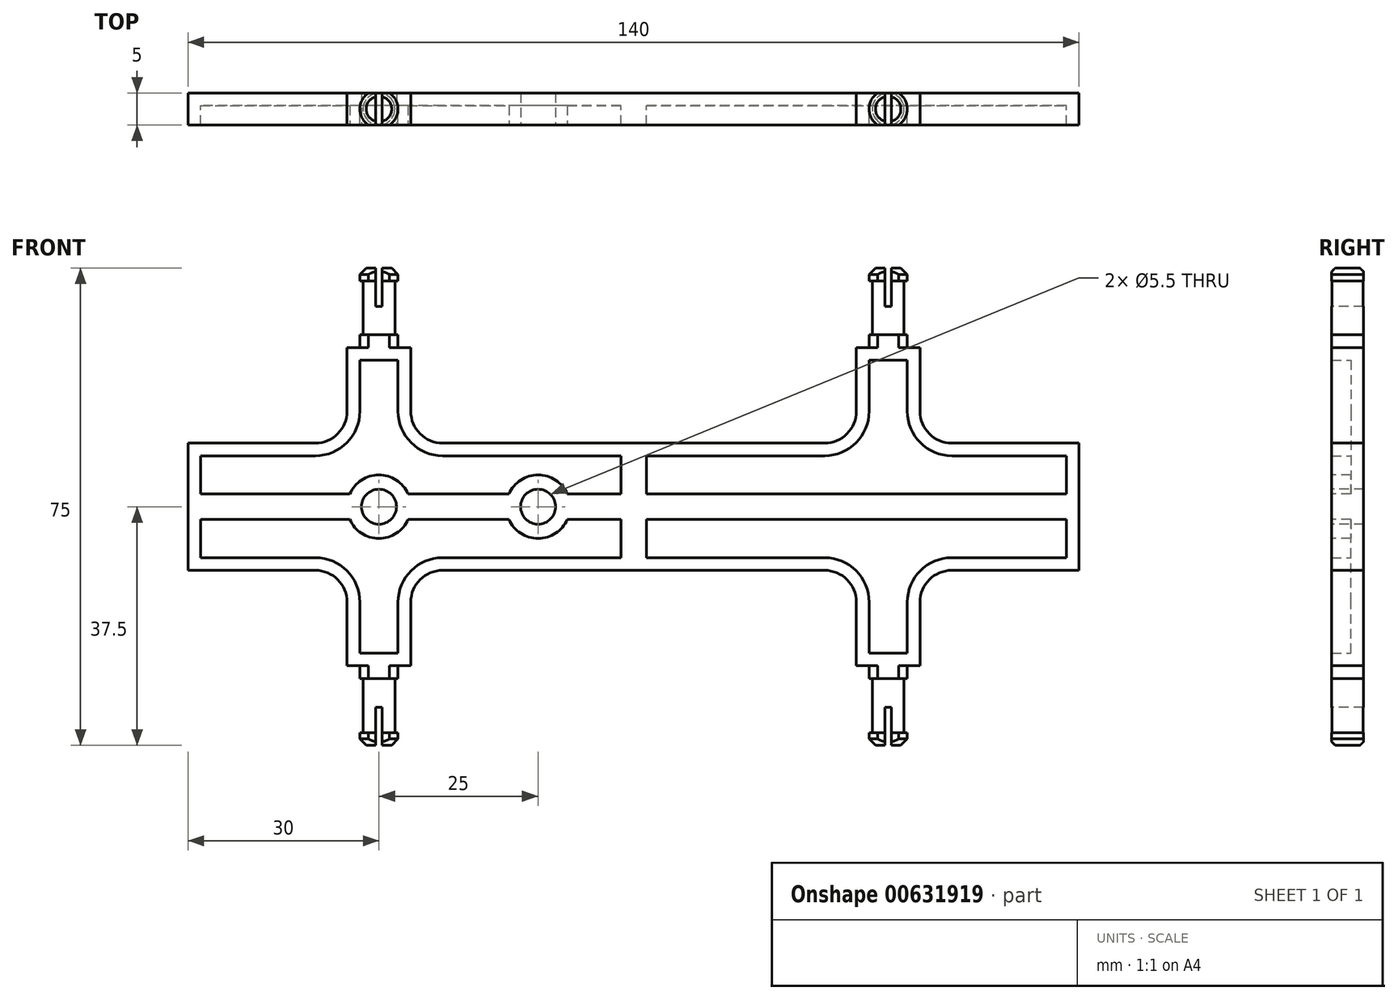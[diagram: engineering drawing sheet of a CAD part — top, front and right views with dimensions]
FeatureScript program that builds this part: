
annotation { "Feature Type Name" : "Feature", "Feature Type Description" : "" }
export const myFeature = defineFeature(function(context is Context, id is Id, definition is map)
    precondition{}
    {
        {
            var Q0;
            Q0=qCreatedBy(makeId("Front.planeOp"),FACE);
            var sketch = newSketch(context, id + "F0", { "sketchPlane" : qUnion([Q0])});
            skLineSegment(sketch, "E0", {"start": v(0, 0) * mm, "end": v(0, 10) * mm});
            skLineSegment(sketch, "E1", {"start": v(0, 10) * mm, "end": v(30, 10) * mm});
            skLineSegment(sketch, "E2", {"start": v(35, 15) * mm, "end": v(35, 25) * mm});
            skLineSegment(sketch, "E3", {"start": v(35, 25) * mm, "end": v(45, 25) * mm});
            skLineSegment(sketch, "E4", {"start": v(45, 25) * mm, "end": v(45, 15) * mm});
            skLineSegment(sketch, "E5", {"start": v(50, 10) * mm, "end": v(70, 10) * mm});
            skLineSegment(sketch, "E6", {"start": v(70, 10) * mm, "end": v(70, 0) * mm});
            skLineSegment(sketch, "E7", {"start": v(70, 0) * mm, "end": v(0, 0) * mm});
            skPoint(sketch, "E8.visualSharp", {"position": v(35, 10) * mm});
            skArc(sketch, "E8.filletArc", {"start": v(30, 10) * mm, "mid": v(33.54, 11.46) * mm, "end": v(35, 15) * mm});
            skPoint(sketch, "E9.visualSharp", {"position": v(45, 10) * mm});
            skArc(sketch, "E9.filletArc", {"start": v(45, 15) * mm, "mid": v(46.46, 11.46) * mm, "end": v(50, 10) * mm});
            skSolve(sketch);
        }
        {
            var Q0;
            Q0 = qSketchRegion(id + "F0", true);
            extrude(context, id + "F1", {"entities" : qUnion([Q0]), "endBound" : BoundingType.SYMMETRIC, "depth" : 5 * mm, "offsetDistance" : 25 * mm});
        }
        {
            var Q0;
            Q0=makeQuery(id+"F1.opExtrude","CAP_FACE",FACE,{"disambiguationData":[OSD([sQuery(id+"F0.wireOp",EDGE,"E0"),sQuery(id+"F0.wireOp",EDGE,"E1"),sQuery(id+"F0.wireOp",EDGE,"E2"),sQuery(id+"F0.wireOp",EDGE,"E3"),sQuery(id+"F0.wireOp",EDGE,"E4"),sQuery(id+"F0.wireOp",EDGE,"E5"),sQuery(id+"F0.wireOp",EDGE,"E6"),sQuery(id+"F0.wireOp",EDGE,"E7"),sQuery(id+"F0.wireOp",EDGE,"E8.filletArc"),sQuery(id+"F0.wireOp",EDGE,"E9.filletArc")])],"isStart":false});
            shell(context, id + "F2", {"entities" : qUnion([Q0]), "thickness" : 2 * mm});
        }
        {
            var Q0;
            Q0=qCreatedBy(makeId("Front.planeOp"),FACE);
            var sketch = newSketch(context, id + "F3", { "sketchPlane" : qUnion([Q0])});
            skLineSegment(sketch, "E10", {"start": v(40, 37.5) * mm, "end": v(37, 37.5) * mm});
            skLineSegment(sketch, "E11", {"start": v(37, 37.5) * mm, "end": v(37, 35.5) * mm});
            skLineSegment(sketch, "E12", {"start": v(37, 35.5) * mm, "end": v(37.5, 35.5) * mm});
            skLineSegment(sketch, "E13", {"start": v(37.5, 35.5) * mm, "end": v(37.5, 27) * mm});
            skLineSegment(sketch, "E14", {"start": v(37.5, 27) * mm, "end": v(37, 27) * mm});
            skLineSegment(sketch, "E15", {"start": v(37, 27) * mm, "end": v(37, 25) * mm});
            skLineSegment(sketch, "E16", {"start": v(37, 25) * mm, "end": v(40, 25) * mm});
            skLineSegment(sketch, "E17", {"start": v(40, 25) * mm, "end": v(40, 37.5) * mm});
            skSolve(sketch);
        }
        {
            var Q0;
            Q0 = qSketchRegion(id + "F3", true);
            var Q1;
            Q1=sQuery(id+"F3.wireOp",EDGE,"E17");
            revolve(context, id + "F4", {"operationType" : NewBodyOperationType.ADD, "entities" : qUnion([Q0]), "axis" : qUnion([Q1]), "revolveType" : RevolveType.FULL});
        }
        {
            var Q0;
            Q0=makeQuery(id+"F4.opRevolve","SWEPT_EDGE",EDGE,{"disambiguationData":[OSD([sQuery(id+"F3.wireOp",EDGE,"E10"),sQuery(id+"F3.wireOp",EDGE,"E11")])]});
            chamfer(context, id + "F5", {"entities" : qUnion([Q0]), "width" : 1 * mm, "tangentPropagation" : true});
        }
        {
            var Q0;
            Q0=makeQuery(id+"F4.opRevolve","SWEPT_FACE",FACE,{"disambiguationData":[OSD([sQuery(id+"F3.wireOp",EDGE,"E10")])]});
            var sketch = newSketch(context, id + "F6", { "sketchPlane" : qUnion([Q0])});
            skLineSegment(sketch, "E18.bottom", {"start": v(-2.12, 2.5) * mm, "end": v(72.88, 2.5) * mm});
            skLineSegment(sketch, "E18.top", {"start": v(-2.12, -2.5) * mm, "end": v(72.88, -2.5) * mm});
            skLineSegment(sketch, "E18.left", {"start": v(-2.12, 2.5) * mm, "end": v(-2.12, -2.5) * mm});
            skLineSegment(sketch, "E18.right", {"start": v(72.88, 2.5) * mm, "end": v(72.88, -2.5) * mm});
            skSolve(sketch);
        }
        {
            var Q0;
            Q0=makeQuery(id+"F6.imprint","IMPRINT",FACE,{"disambiguationData":[TD([[makeQuery(id+"F6.imprint","IMPRINT",EDGE,{"derivedFrom":sQuery(id+"F6.wireOp",EDGE,"E18.bottom")}),-1.0]])]});
            var Q1;
            {var subQ0=sQuery(id+"F3.wireOp",EDGE,"E10");Q1=makeQuery(id+"F6.imprint","IMPRINT",FACE,{"disambiguationData":[TD([[makeQuery(id+"F6.imprint","IMPRINT",EDGE,{"derivedFrom":makeQuery(id+"F5.opChamfer","BLEND_EDGE",EDGE,{"blendedFrom":[makeQuery(id+"F4.opRevolve","SWEPT_EDGE",EDGE,{"disambiguationData":[OSD([subQ0,sQuery(id+"F3.wireOp",EDGE,"E11")])]}),makeQuery(id+"F4.opRevolve","SWEPT_FACE",FACE,{"disambiguationData":[OSD([subQ0])]})],"blendedInto":[makeQuery(id+"F4.opRevolve","SWEPT_FACE",FACE,{"disambiguationData":[OSD([subQ0])]})]})}),1.0]])]});}
            extrude(context, id + "F7", {"entities" : qUnion([Q0, Q1]), "operationType" : NewBodyOperationType.INTERSECT, "endBound" : BoundingType.THROUGH_ALL, "oppositeDirection" : true, "depth" : 25 * mm, "offsetDistance" : 25 * mm});
        }
        {
            var Q0;
            Q0=makeQuery(id+"F4.opRevolve","SWEPT_FACE",FACE,{"disambiguationData":[OSD([sQuery(id+"F3.wireOp",EDGE,"E10")])]});
            var sketch = newSketch(context, id + "F8", { "sketchPlane" : qUnion([Q0])});
            skLineSegment(sketch, "E19.bottom", {"start": v(39.5, 3.76) * mm, "end": v(40.5, 3.76) * mm});
            skLineSegment(sketch, "E19.top", {"start": v(39.5, -4.19) * mm, "end": v(40.5, -4.19) * mm});
            skLineSegment(sketch, "E19.left", {"start": v(39.5, 3.76) * mm, "end": v(39.5, -4.19) * mm});
            skLineSegment(sketch, "E19.right", {"start": v(40.5, 3.76) * mm, "end": v(40.5, -4.19) * mm});
            skSolve(sketch);
        }
        {
            var Q0;
            Q0 = qSketchRegion(id + "F8", true);
            extrude(context, id + "F9", {"entities" : qUnion([Q0]), "operationType" : NewBodyOperationType.REMOVE, "oppositeDirection" : true, "depth" : 6 * mm, "offsetDistance" : 25 * mm});
        }
        {
            var Q0;
            Q0=makeQuery(id+"F1.opExtrude","SWEPT_BODY",BODY,{"disambiguationData":[OSD([sQuery(id+"F0.wireOp",EDGE,"E0"),sQuery(id+"F0.wireOp",EDGE,"E1"),sQuery(id+"F0.wireOp",EDGE,"E2"),sQuery(id+"F0.wireOp",EDGE,"E3"),sQuery(id+"F0.wireOp",EDGE,"E4"),sQuery(id+"F0.wireOp",EDGE,"E5"),sQuery(id+"F0.wireOp",EDGE,"E6"),sQuery(id+"F0.wireOp",EDGE,"E7"),sQuery(id+"F0.wireOp",EDGE,"E8.filletArc"),sQuery(id+"F0.wireOp",EDGE,"E9.filletArc")])]});
            var Q1;
            Q1=qCreatedBy(makeId("Top.planeOp"),FACE);
            mirror(context, id + "F10", {"operationType" : NewBodyOperationType.ADD, "entities" : qUnion([Q0]), "mirrorPlane" : qUnion([Q1])});
        }
        {
            var Q0;
            Q0=makeQuery(id+"F1.opExtrude","SWEPT_BODY",BODY,{"disambiguationData":[OSD([sQuery(id+"F0.wireOp",EDGE,"E0"),sQuery(id+"F0.wireOp",EDGE,"E1"),sQuery(id+"F0.wireOp",EDGE,"E2"),sQuery(id+"F0.wireOp",EDGE,"E3"),sQuery(id+"F0.wireOp",EDGE,"E4"),sQuery(id+"F0.wireOp",EDGE,"E5"),sQuery(id+"F0.wireOp",EDGE,"E6"),sQuery(id+"F0.wireOp",EDGE,"E7"),sQuery(id+"F0.wireOp",EDGE,"E8.filletArc"),sQuery(id+"F0.wireOp",EDGE,"E9.filletArc")])]});
            var Q1;
            Q1=qCreatedBy(makeId("Right.planeOp"),FACE);
            mirror(context, id + "F11", {"operationType" : NewBodyOperationType.ADD, "entities" : qUnion([Q0]), "mirrorPlane" : qUnion([Q1])});
        }
        {
            var Q0;
            {var subQ0=makeQuery(id+"F7.boolean.opBoolean","MERGE",FACE,{"derivedFrom":[makeQuery(id+"F1.opExtrude","CAP_FACE",FACE,{"disambiguationData":[OSD([sQuery(id+"F0.wireOp",EDGE,"E0"),sQuery(id+"F0.wireOp",EDGE,"E1"),sQuery(id+"F0.wireOp",EDGE,"E2"),sQuery(id+"F0.wireOp",EDGE,"E3"),sQuery(id+"F0.wireOp",EDGE,"E4"),sQuery(id+"F0.wireOp",EDGE,"E5"),sQuery(id+"F0.wireOp",EDGE,"E6"),sQuery(id+"F0.wireOp",EDGE,"E7"),sQuery(id+"F0.wireOp",EDGE,"E8.filletArc"),sQuery(id+"F0.wireOp",EDGE,"E9.filletArc")])],"isStart":false}),makeQuery(id+"F7.boolean.toolComplement.opBoolean","COPY",FACE,{"derivedFrom":makeQuery(id+"F7.opExtrude","SWEPT_FACE",FACE,{"disambiguationData":[OSD([sQuery(id+"F6.wireOp",EDGE,"E18.top")])]})})]});var subQ1=makeQuery(id+"F10.boolean.opBoolean","MERGE",FACE,{"derivedFrom":[subQ0,makeQuery(id+"F10.opPattern","COPY",FACE,{"derivedFrom":subQ0,"instanceName":"1"})]});Q0=makeQuery(id+"F11.boolean.opBoolean","MERGE",FACE,{"derivedFrom":[subQ1,makeQuery(id+"F11.opPattern","COPY",FACE,{"derivedFrom":subQ1,"instanceName":"1"})]});}
            var sketch = newSketch(context, id + "F12", { "sketchPlane" : qUnion([Q0])});
            skCircle(sketch, "E20", {"center": v(-40, 0) * mm, "radius": 5 * mm});
            skCircle(sketch, "E21", {"center": v(-15, 0) * mm, "radius": 5 * mm});
            skSolve(sketch);
        }
        {
            var Q0;
            Q0 = qSketchRegion(id + "F12", true);
            extrude(context, id + "F13", {"entities" : qUnion([Q0]), "operationType" : NewBodyOperationType.ADD, "endBound" : BoundingType.UP_TO_NEXT, "oppositeDirection" : true, "depth" : 25 * mm, "offsetDistance" : 25 * mm});
        }
        {
            var Q0;
            {var subQ0=makeQuery(id+"F7.boolean.opBoolean","MERGE",FACE,{"derivedFrom":[makeQuery(id+"F1.opExtrude","CAP_FACE",FACE,{"disambiguationData":[OSD([sQuery(id+"F0.wireOp",EDGE,"E0"),sQuery(id+"F0.wireOp",EDGE,"E1"),sQuery(id+"F0.wireOp",EDGE,"E2"),sQuery(id+"F0.wireOp",EDGE,"E3"),sQuery(id+"F0.wireOp",EDGE,"E4"),sQuery(id+"F0.wireOp",EDGE,"E5"),sQuery(id+"F0.wireOp",EDGE,"E6"),sQuery(id+"F0.wireOp",EDGE,"E7"),sQuery(id+"F0.wireOp",EDGE,"E8.filletArc"),sQuery(id+"F0.wireOp",EDGE,"E9.filletArc")])],"isStart":false}),makeQuery(id+"F7.boolean.toolComplement.opBoolean","COPY",FACE,{"derivedFrom":makeQuery(id+"F7.opExtrude","SWEPT_FACE",FACE,{"disambiguationData":[OSD([sQuery(id+"F6.wireOp",EDGE,"E18.top")])]})})]});var subQ1=makeQuery(id+"F10.boolean.opBoolean","MERGE",FACE,{"derivedFrom":[subQ0,makeQuery(id+"F10.opPattern","COPY",FACE,{"derivedFrom":subQ0,"instanceName":"1"})]});Q0=makeQuery(id+"F13.boolean.opBoolean","MERGE",FACE,{"derivedFrom":[makeQuery(id+"F11.boolean.opBoolean","MERGE",FACE,{"derivedFrom":[subQ1,makeQuery(id+"F11.opPattern","COPY",FACE,{"derivedFrom":subQ1,"instanceName":"1"})]}),makeQuery(id+"F13.opExtrude","CAP_FACE",FACE,{"disambiguationData":[OSD([sQuery(id+"F12.wireOp",EDGE,"E20")])],"isStart":true}),makeQuery(id+"F13.opExtrude","CAP_FACE",FACE,{"disambiguationData":[OSD([sQuery(id+"F12.wireOp",EDGE,"E21")])],"isStart":true})]});}
            var sketch = newSketch(context, id + "F14", { "sketchPlane" : qUnion([Q0])});
            skPoint(sketch, "E22", {"position": v(-40, 0) * mm});
            skPoint(sketch, "E23", {"position": v(-15, 0) * mm});
            skSolve(sketch);
        }
        {
            var Q0;
            Q0=sQuery(id+"F14.wireOp",VERTEX,"E22");
            var Q1;
            Q1=sQuery(id+"F14.wireOp",VERTEX,"E23");
            var Q2;
            Q2=makeQuery(id+"F1.opExtrude","SWEPT_BODY",BODY,{"disambiguationData":[OSD([sQuery(id+"F0.wireOp",EDGE,"E0"),sQuery(id+"F0.wireOp",EDGE,"E1"),sQuery(id+"F0.wireOp",EDGE,"E2"),sQuery(id+"F0.wireOp",EDGE,"E3"),sQuery(id+"F0.wireOp",EDGE,"E4"),sQuery(id+"F0.wireOp",EDGE,"E5"),sQuery(id+"F0.wireOp",EDGE,"E6"),sQuery(id+"F0.wireOp",EDGE,"E7"),sQuery(id+"F0.wireOp",EDGE,"E8.filletArc"),sQuery(id+"F0.wireOp",EDGE,"E9.filletArc")])]});
            hole(context, id + "F15", {"style" : HoleStyle.SIMPLE, "endStyle" : HoleEndStyle.THROUGH, "holeDiameter" : 5.5 * mm, "majorDiameter" : 5 * mm, "isTappedThrough" : true, "tappedDepth" : 12 * mm, "tapClearance" : 3, "startFromSketch" : true, "locations" : qUnion([Q0, Q1]), "scope" : qUnion([Q2])});
        }
    });
